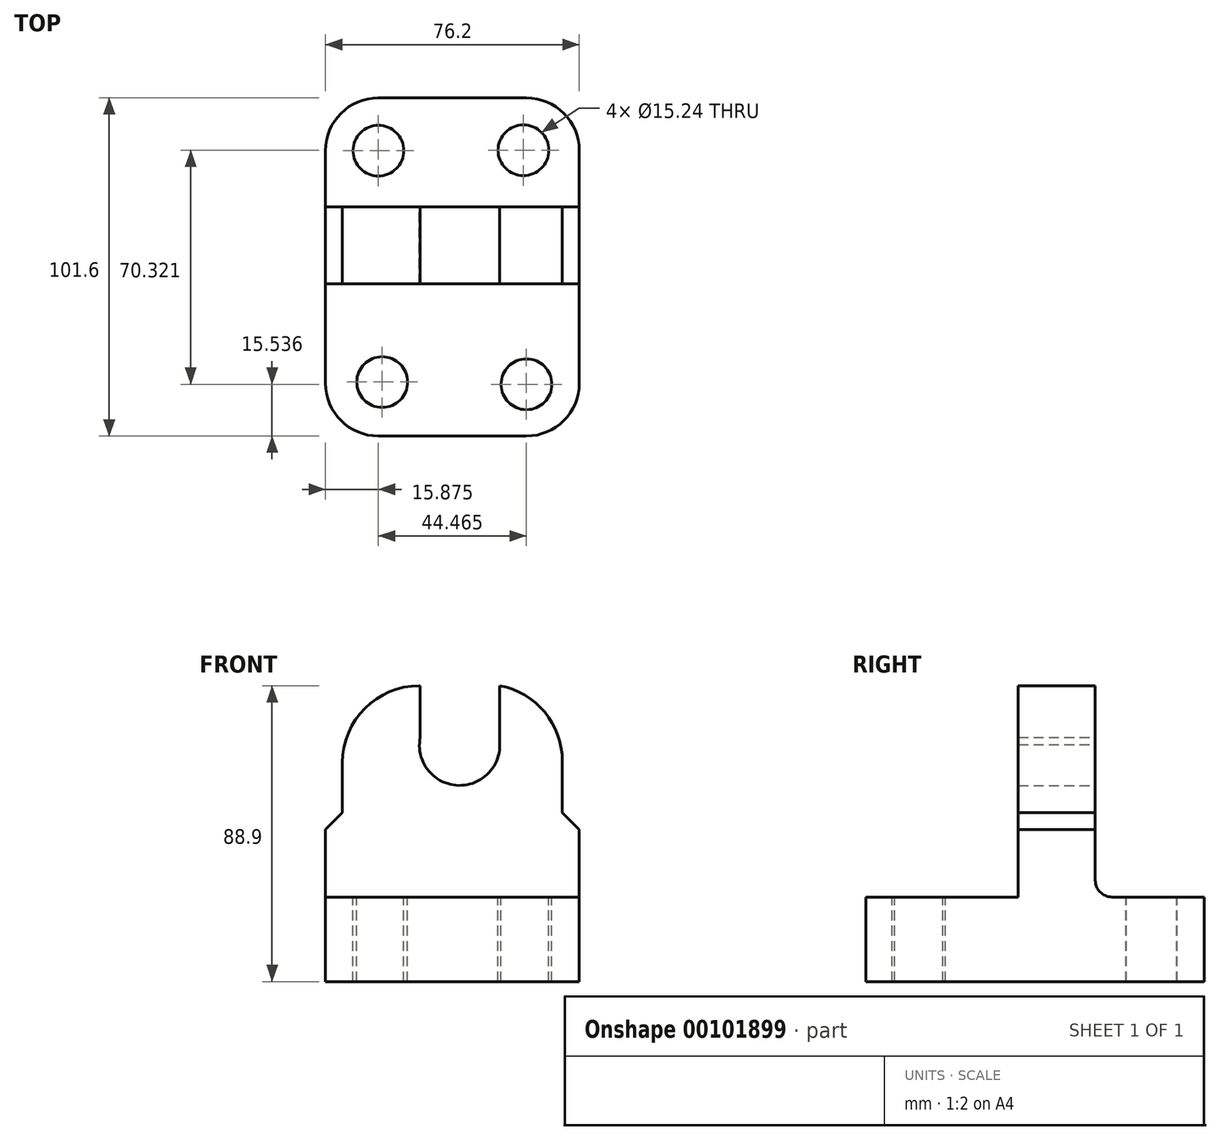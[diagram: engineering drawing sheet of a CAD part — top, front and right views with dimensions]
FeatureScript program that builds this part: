
annotation { "Feature Type Name" : "Feature", "Feature Type Description" : "" }
export const myFeature = defineFeature(function(context is Context, id is Id, definition is map)
    precondition{}
    {
        {
            var Q0;
            Q0=qCreatedBy(makeId("Top.planeOp"),FACE);
            var sketch = newSketch(context, id + "F0", { "sketchPlane" : qUnion([Q0])});
            skLineSegment(sketch, "E0.bottom", {"start": v(0, 0) * mm, "end": v(76.2, 0) * mm});
            skLineSegment(sketch, "E0.top", {"start": v(0, 101.6) * mm, "end": v(76.2, 101.6) * mm});
            skLineSegment(sketch, "E0.left", {"start": v(0, 0) * mm, "end": v(0, 101.6) * mm});
            skLineSegment(sketch, "E0.right", {"start": v(76.2, 0) * mm, "end": v(76.2, 101.6) * mm});
            skSolve(sketch);
        }
        {
            var Q0;
            Q0=makeQuery(id+"F0.imprint","IMPRINT",FACE,{"disambiguationData":[TD([[makeQuery(id+"F0.imprint","IMPRINT",EDGE,{"derivedFrom":sQuery(id+"F0.wireOp",EDGE,"E0.bottom")}),1.0]])]});
            extrude(context, id + "F1", {"entities" : qUnion([Q0]), "depth" : 25.4 * mm});
        }
        {
            var Q0;
            Q0=makeQuery(id+"F1.opExtrude","SWEPT_EDGE",EDGE,{"disambiguationData":[OSD([sQuery(id+"F0.wireOp",EDGE,"E0.top"),sQuery(id+"F0.wireOp",EDGE,"E0.left")])]});
            var Q1;
            Q1=makeQuery(id+"F1.opExtrude","SWEPT_EDGE",EDGE,{"disambiguationData":[OSD([sQuery(id+"F0.wireOp",EDGE,"E0.bottom"),sQuery(id+"F0.wireOp",EDGE,"E0.left")])]});
            var Q2;
            Q2=makeQuery(id+"F1.opExtrude","SWEPT_EDGE",EDGE,{"disambiguationData":[OSD([sQuery(id+"F0.wireOp",EDGE,"E0.bottom"),sQuery(id+"F0.wireOp",EDGE,"E0.right")])]});
            var Q3;
            Q3=makeQuery(id+"F1.opExtrude","SWEPT_EDGE",EDGE,{"disambiguationData":[OSD([sQuery(id+"F0.wireOp",EDGE,"E0.top"),sQuery(id+"F0.wireOp",EDGE,"E0.right")])]});
            fillet(context, id + "F2", {"entities" : qUnion([Q0, Q1, Q2, Q3]), "radius" : 15.88 * mm, "tangentPropagation" : true, "allowEdgeOverflow" : false});
        }
        {
            var Q0;
            Q0=makeQuery(id+"F1.opExtrude","CAP_FACE",FACE,{"disambiguationData":[OSD([sQuery(id+"F0.wireOp",EDGE,"E0.bottom"),sQuery(id+"F0.wireOp",EDGE,"E0.top"),sQuery(id+"F0.wireOp",EDGE,"E0.left"),sQuery(id+"F0.wireOp",EDGE,"E0.right")])],"isStart":false});
            var sketch = newSketch(context, id + "F3", { "sketchPlane" : qUnion([Q0])});
            skCircle(sketch, "E1", {"center": v(15.87, 85.72) * mm, "radius": 7.25 * mm});
            skSolve(sketch);
        }
        {
            var Q0;
            Q0=makeQuery(id+"F1.opExtrude","CAP_FACE",FACE,{"disambiguationData":[OSD([sQuery(id+"F0.wireOp",EDGE,"E0.bottom"),sQuery(id+"F0.wireOp",EDGE,"E0.top"),sQuery(id+"F0.wireOp",EDGE,"E0.left"),sQuery(id+"F0.wireOp",EDGE,"E0.right")])],"isStart":false});
            var sketch = newSketch(context, id + "F4", { "sketchPlane" : qUnion([Q0])});
            skCircle(sketch, "E2", {"center": v(59.43, 85.86) * mm, "radius": 7.25 * mm});
            skSolve(sketch);
        }
        {
            var Q0;
            Q0=makeQuery(id+"F1.opExtrude","CAP_FACE",FACE,{"disambiguationData":[OSD([sQuery(id+"F0.wireOp",EDGE,"E0.bottom"),sQuery(id+"F0.wireOp",EDGE,"E0.top"),sQuery(id+"F0.wireOp",EDGE,"E0.left"),sQuery(id+"F0.wireOp",EDGE,"E0.right")])],"isStart":false});
            var sketch = newSketch(context, id + "F5", { "sketchPlane" : qUnion([Q0])});
            skCircle(sketch, "E3", {"center": v(17.01, 16.22) * mm, "radius": 7.25 * mm});
            skSolve(sketch);
        }
        {
            var Q0;
            Q0=makeQuery(id+"F1.opExtrude","CAP_FACE",FACE,{"disambiguationData":[OSD([sQuery(id+"F0.wireOp",EDGE,"E0.bottom"),sQuery(id+"F0.wireOp",EDGE,"E0.top"),sQuery(id+"F0.wireOp",EDGE,"E0.left"),sQuery(id+"F0.wireOp",EDGE,"E0.right")])],"isStart":false});
            var sketch = newSketch(context, id + "F6", { "sketchPlane" : qUnion([Q0])});
            skCircle(sketch, "E4", {"center": v(60.34, 15.54) * mm, "radius": 7.25 * mm});
            skSolve(sketch);
        }
        {
            var Q0;
            Q0=sQuery(id+"F3.wireOp",VERTEX,"E1.center");
            var Q1;
            Q1=sQuery(id+"F4.wireOp",VERTEX,"E2.center");
            var Q2;
            Q2=sQuery(id+"F5.wireOp",VERTEX,"E3.center");
            var Q3;
            Q3=sQuery(id+"F6.wireOp",VERTEX,"E4.center");
            var Q4;
            Q4=makeQuery(id+"F1.opExtrude","SWEPT_BODY",BODY,{"disambiguationData":[OSD([sQuery(id+"F0.wireOp",EDGE,"E0.bottom"),sQuery(id+"F0.wireOp",EDGE,"E0.top"),sQuery(id+"F0.wireOp",EDGE,"E0.left"),sQuery(id+"F0.wireOp",EDGE,"E0.right")])]});
            hole(context, id + "F7", {"style" : HoleStyle.SIMPLE, "endStyle" : HoleEndStyle.THROUGH, "holeDiameter" : 15.24 * mm, "locations" : qUnion([Q0, Q1, Q2, Q3]), "scope" : qUnion([Q4]), "isTappedThrough" : true});
        }
        {
            var Q0;
            Q0=makeQuery(id+"F1.opExtrude","CAP_FACE",FACE,{"disambiguationData":[OSD([sQuery(id+"F0.wireOp",EDGE,"E0.bottom"),sQuery(id+"F0.wireOp",EDGE,"E0.top"),sQuery(id+"F0.wireOp",EDGE,"E0.left"),sQuery(id+"F0.wireOp",EDGE,"E0.right")])],"isStart":false});
            var sketch = newSketch(context, id + "F8", { "sketchPlane" : qUnion([Q0])});
            skLineSegment(sketch, "E5.bottom", {"start": v(0, 68.87) * mm, "end": v(76.2, 68.87) * mm});
            skLineSegment(sketch, "E5.top", {"start": v(0, 45.76) * mm, "end": v(76.2, 45.76) * mm});
            skLineSegment(sketch, "E5.left", {"start": v(0, 68.87) * mm, "end": v(0, 45.76) * mm});
            skLineSegment(sketch, "E5.right", {"start": v(76.2, 68.87) * mm, "end": v(76.2, 45.76) * mm});
            skSolve(sketch);
        }
        {
            var Q0;
            Q0 = qSketchRegion(id + "F8", true);
            extrude(context, id + "F9", {"entities" : qUnion([Q0]), "operationType" : NewBodyOperationType.ADD, "depth" : 25.4 * mm});
        }
        {
            var Q0;
            Q0=makeQuery(id+"F9.opExtrude","CAP_EDGE",EDGE,{"disambiguationData":[OSD([sQuery(id+"F8.wireOp",EDGE,"E5.top")])],"isStart":true});
            var Q1;
            Q1=makeQuery(id+"F9.opExtrude","CAP_EDGE",EDGE,{"disambiguationData":[OSD([sQuery(id+"F8.wireOp",EDGE,"E5.bottom")])],"isStart":true});
            fillet(context, id + "F10", {"entities" : qUnion([Q0, Q1]), "radius" : 5.08 * mm, "tangentPropagation" : true, "allowEdgeOverflow" : false});
        }
        {
            var Q0;
            Q0=makeQuery(id+"F9.opExtrude","CAP_EDGE",EDGE,{"disambiguationData":[OSD([sQuery(id+"F8.wireOp",EDGE,"E5.left")])],"isStart":false});
            var Q1;
            Q1=makeQuery(id+"F9.opExtrude","CAP_EDGE",EDGE,{"disambiguationData":[OSD([sQuery(id+"F8.wireOp",EDGE,"E5.right")])],"isStart":false});
            chamfer(context, id + "F11", {"entities" : qUnion([Q0, Q1]), "width" : 5.08 * mm, "tangentPropagation" : true});
        }
        {
            var Q0;
            Q0=makeQuery(id+"F9.opExtrude","CAP_FACE",FACE,{"disambiguationData":[OSD([sQuery(id+"F8.wireOp",EDGE,"E5.bottom"),sQuery(id+"F8.wireOp",EDGE,"E5.top"),sQuery(id+"F8.wireOp",EDGE,"E5.left"),sQuery(id+"F8.wireOp",EDGE,"E5.right")])],"isStart":false});
            var sketch = newSketch(context, id + "F12", { "sketchPlane" : qUnion([Q0])});
            skLineSegment(sketch, "E6.bottom", {"start": v(71.12, 68.87) * mm, "end": v(5.08, 68.87) * mm});
            skLineSegment(sketch, "E6.top", {"start": v(71.12, 45.76) * mm, "end": v(5.08, 45.76) * mm});
            skLineSegment(sketch, "E6.left", {"start": v(71.12, 68.87) * mm, "end": v(71.12, 45.76) * mm});
            skLineSegment(sketch, "E6.right", {"start": v(5.08, 68.87) * mm, "end": v(5.08, 45.76) * mm});
            skSolve(sketch);
        }
        {
            var Q0;
            Q0 = qSketchRegion(id + "F12", true);
            var Q1;
            Q1=makeQuery(id+"F9.opExtrude","CAP_FACE",FACE,{"disambiguationData":[OSD([sQuery(id+"F8.wireOp",EDGE,"E5.bottom"),sQuery(id+"F8.wireOp",EDGE,"E5.top"),sQuery(id+"F8.wireOp",EDGE,"E5.left"),sQuery(id+"F8.wireOp",EDGE,"E5.right")])],"isStart":false});
            extrude(context, id + "F13", {"entities" : qUnion([Q0, Q1]), "operationType" : NewBodyOperationType.ADD, "depth" : 38.1 * mm});
        }
        {
            var Q0;
            {var subQ0=sQuery(id+"F8.wireOp",EDGE,"E5.bottom");Q0=makeQuery(id+"F13.boolean.opBoolean","MERGE",FACE,{"derivedFrom":[makeQuery(id+"F9.opExtrude","SWEPT_FACE",FACE,{"disambiguationData":[OSD([subQ0])]}),makeQuery(id+"F13.opExtrude","SWEPT_FACE",FACE,{"disambiguationData":[OSD([subQ0])]})]});}
            var sketch = newSketch(context, id + "F14", { "sketchPlane" : qUnion([Q0])});
            skCircle(sketch, "E7", {"center": v(-40.27, 71) * mm, "radius": 12.15 * mm});
            skSolve(sketch);
        }
        {
            var Q0;
            Q0=sQuery(id+"F14.wireOp",VERTEX,"E7.center");
            var Q1;
            Q1=makeQuery(id+"F1.opExtrude","SWEPT_BODY",BODY,{"disambiguationData":[OSD([sQuery(id+"F0.wireOp",EDGE,"E0.bottom"),sQuery(id+"F0.wireOp",EDGE,"E0.top"),sQuery(id+"F0.wireOp",EDGE,"E0.left"),sQuery(id+"F0.wireOp",EDGE,"E0.right")])]});
            hole(context, id + "F15", {"style" : HoleStyle.SIMPLE, "endStyle" : HoleEndStyle.THROUGH, "holeDiameter" : 24.13 * mm, "locations" : qUnion([Q0]), "scope" : qUnion([Q1]), "isTappedThrough" : true});
        }
        {
            var Q0;
            {var subQ0=sQuery(id+"F8.wireOp",EDGE,"E5.bottom");Q0=makeQuery(id+"F13.boolean.opBoolean","MERGE",FACE,{"derivedFrom":[makeQuery(id+"F9.opExtrude","SWEPT_FACE",FACE,{"disambiguationData":[OSD([subQ0])]}),makeQuery(id+"F13.opExtrude","SWEPT_FACE",FACE,{"disambiguationData":[OSD([subQ0])]})]});}
            var sketch = newSketch(context, id + "F16", { "sketchPlane" : qUnion([Q0])});
            skLineSegment(sketch, "E8.bottom", {"start": v(-52.33, 71.22) * mm, "end": v(-28.44, 71.22) * mm});
            skLineSegment(sketch, "E8.top", {"start": v(-52.33, 88.9) * mm, "end": v(-28.44, 88.9) * mm});
            skLineSegment(sketch, "E8.left", {"start": v(-52.33, 71.22) * mm, "end": v(-52.33, 88.9) * mm});
            skLineSegment(sketch, "E8.right", {"start": v(-28.44, 71.22) * mm, "end": v(-28.44, 88.9) * mm});
            skSolve(sketch);
        }
        {
            var Q0;
            Q0 = qSketchRegion(id + "F16", true);
            extrude(context, id + "F17", {"entities" : qUnion([Q0]), "operationType" : NewBodyOperationType.REMOVE, "oppositeDirection" : true, "depth" : 58.9 * mm});
        }
        {
            var Q0;
            {var subQ0=sQuery(id+"F8.wireOp",EDGE,"E5.right");var subQ1=sQuery(id+"F8.wireOp",EDGE,"E5.left");var subQ2=sQuery(id+"F8.wireOp",EDGE,"E5.top");var subQ3=sQuery(id+"F8.wireOp",EDGE,"E5.bottom");Q0=makeQuery(id+"F13.opExtrude","CAP_EDGE",EDGE,{"disambiguationData":[OSD([subQ3,subQ2,subQ1,subQ0]),TDD([makeQuery(id+"F11.opChamfer","BLEND_EDGE",EDGE,{"blendedFrom":[makeQuery(id+"F9.opExtrude","CAP_EDGE",EDGE,{"disambiguationData":[OSD([subQ0])],"isStart":false}),makeQuery(id+"F9.opExtrude","CAP_FACE",FACE,{"disambiguationData":[OSD([subQ3,subQ2,subQ1,subQ0])],"isStart":false})],"blendedInto":[makeQuery(id+"F9.opExtrude","CAP_FACE",FACE,{"disambiguationData":[OSD([subQ3,subQ2,subQ1,subQ0])],"isStart":false})]})])],"isStart":false});}
            var Q1;
            {var subQ0=sQuery(id+"F8.wireOp",EDGE,"E5.right");var subQ1=sQuery(id+"F8.wireOp",EDGE,"E5.left");var subQ2=sQuery(id+"F8.wireOp",EDGE,"E5.top");var subQ3=sQuery(id+"F8.wireOp",EDGE,"E5.bottom");Q1=makeQuery(id+"F13.opExtrude","CAP_EDGE",EDGE,{"disambiguationData":[OSD([subQ3,subQ2,subQ1,subQ0]),TDD([makeQuery(id+"F11.opChamfer","BLEND_EDGE",EDGE,{"blendedFrom":[makeQuery(id+"F9.opExtrude","CAP_EDGE",EDGE,{"disambiguationData":[OSD([subQ1])],"isStart":false}),makeQuery(id+"F9.opExtrude","CAP_FACE",FACE,{"disambiguationData":[OSD([subQ3,subQ2,subQ1,subQ0])],"isStart":false})],"blendedInto":[makeQuery(id+"F9.opExtrude","CAP_FACE",FACE,{"disambiguationData":[OSD([subQ3,subQ2,subQ1,subQ0])],"isStart":false})]})])],"isStart":false});}
            fillet(context, id + "F18", {"entities" : qUnion([Q0, Q1]), "radius" : 23.12 * mm, "tangentPropagation" : true, "allowEdgeOverflow" : false});
        }
    });
